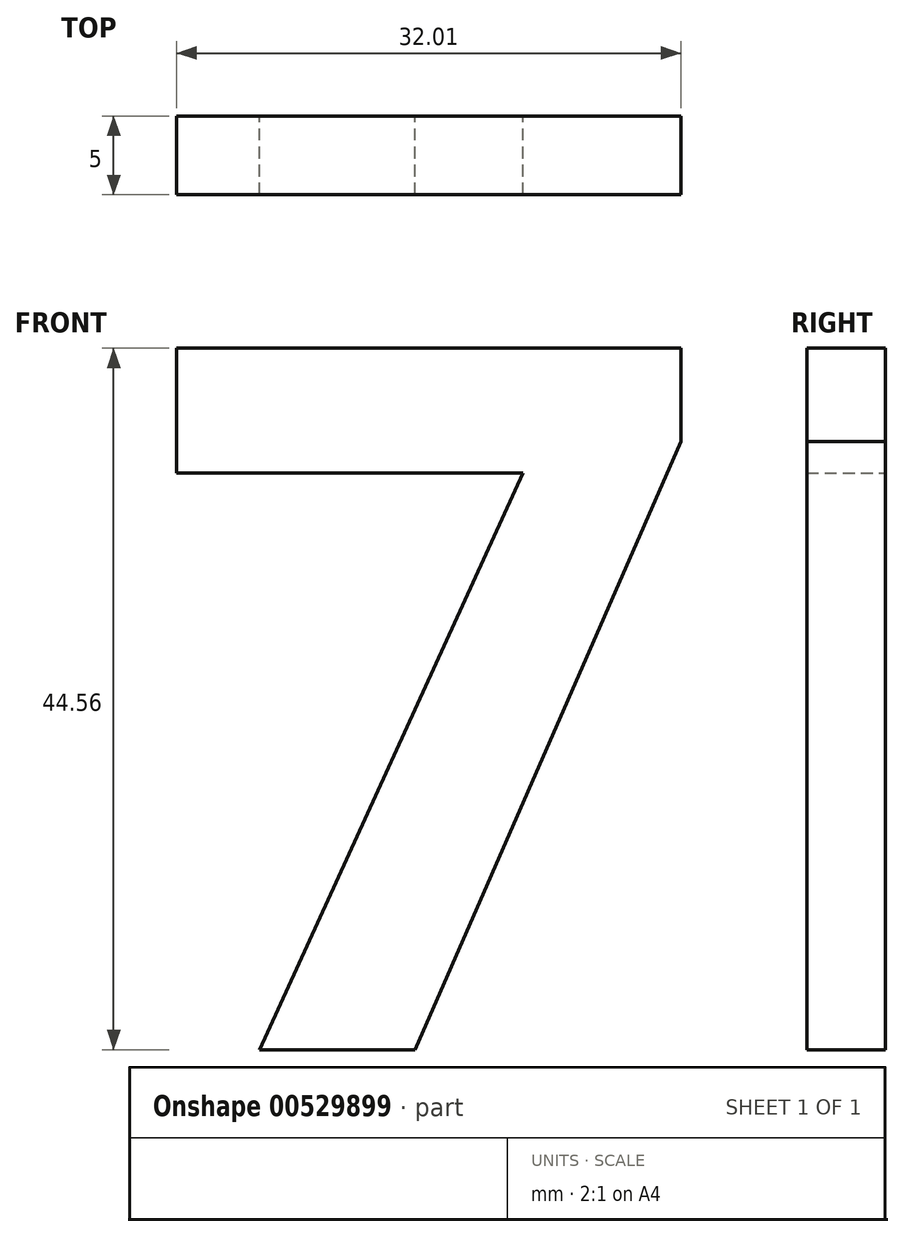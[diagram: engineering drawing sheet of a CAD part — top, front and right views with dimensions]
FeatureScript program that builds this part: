
annotation { "Feature Type Name" : "Feature", "Feature Type Description" : "" }
export const myFeature = defineFeature(function(context is Context, id is Id, definition is map)
    precondition{}
    {
        {
            var Q0;
            Q0=qCreatedBy(makeId("Front.planeOp"),FACE);
            var sketch = newSketch(context, id + "F0", { "sketchPlane" : qUnion([Q0])});
            skText(sketch, "E0", { "text": "7", "fontName": "OpenSans-Bold.ttf"});
            const initialGuessF0  = {"E0": [-0.05358, 0.01322, 1, 0, 0.045]};
            skSetInitialGuess(sketch, initialGuessF0);
            skSolve(sketch);
        }
        {
            var Q0;
            Q0=makeQuery(id+"F0.imprint","IMPRINT",FACE,{"disambiguationData":[TD([[makeQuery(id+"F0.imprint","IMPRINT",EDGE,{"derivedFrom":sQuery(id+"F0.wireOp",EDGE,"E0.sketch_text.stroke-0")}),-1.0]])]});
            extrude(context, id + "F1", {"entities" : qUnion([Q0]), "depth" : 5 * mm, "offsetDistance" : 25 * mm});
        }
    });
